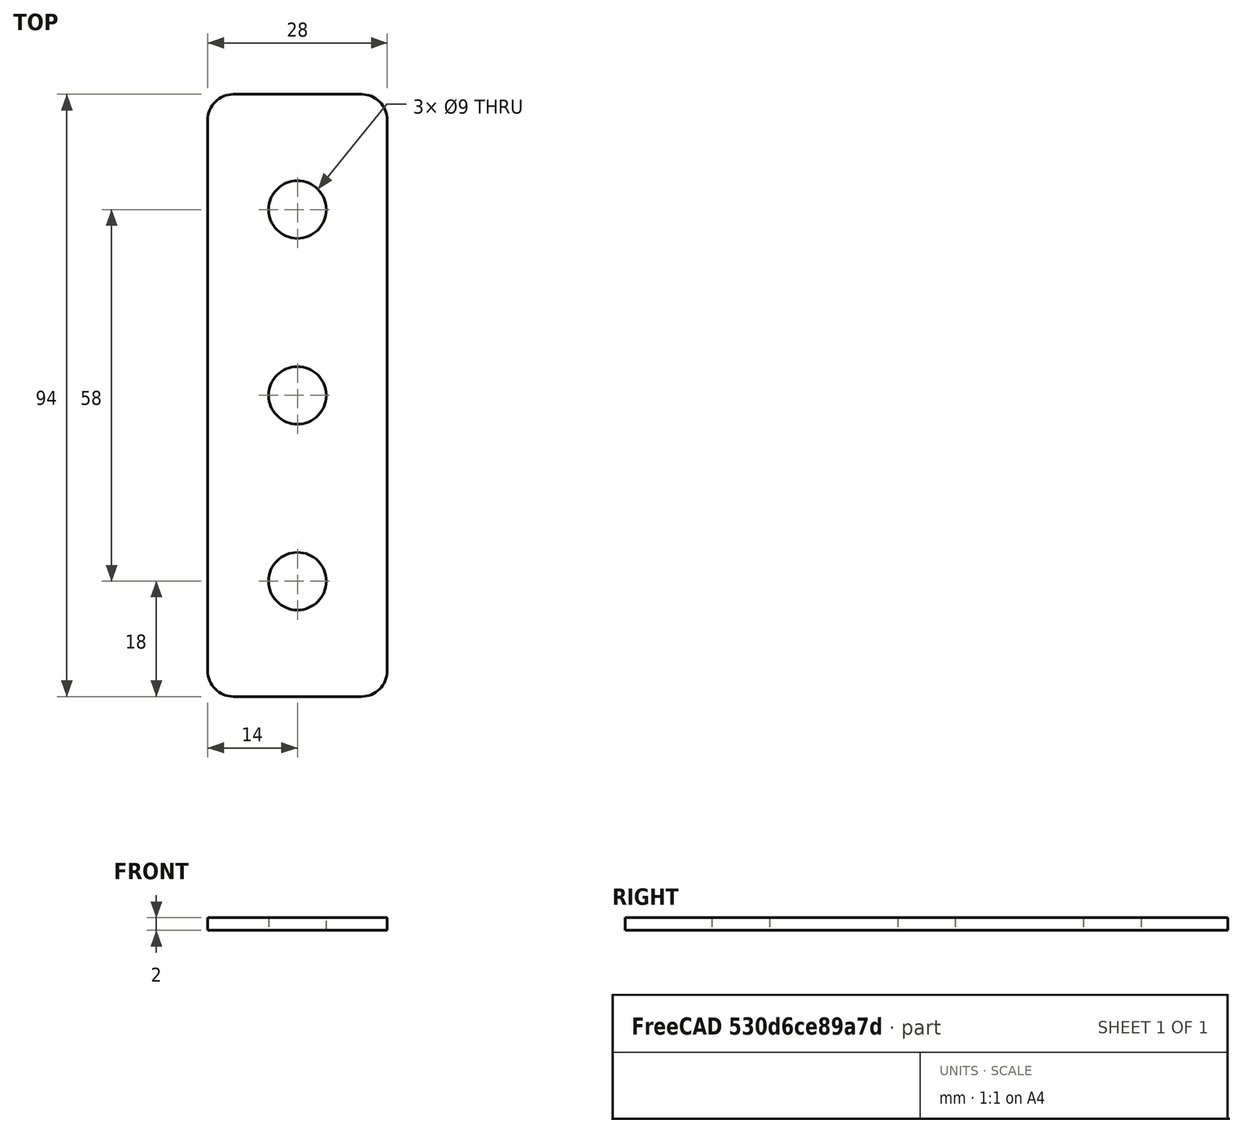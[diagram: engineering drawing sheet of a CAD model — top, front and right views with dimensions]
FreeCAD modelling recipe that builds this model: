
FCSTD DOCUMENT  (FreeCAD 0.21R33694 (Git))
Label: GabaritoCorteBorracha1
License: All rights reserved
LicenseURL: http://en.wikipedia.org/wiki/All_rights_reserved
objects: Sketcher::SketchObject×1, PartDesign::Pad×1, PartDesign::Body×1
note: 4 computed .brp shape members not serialized (recipe doc carries the construction recipe); baked Part::Feature solids carry a one-line shape summary decoded from their .brp

FEATURE [Sketcher::SketchObject] Sketch
  FullyConstrained = true
  MapMode = 5
  Support = -> [XY_Plane]
  sketch-geometry (11):
    g0: LineSegment StartX=-10 StartY=47 StartZ=0 EndX=10 EndY=47 EndZ=0
    g1: LineSegment StartX=14 StartY=43 StartZ=0 EndX=14 EndY=-43 EndZ=0
    g2: LineSegment StartX=10 StartY=-47 StartZ=0 EndX=-10 EndY=-47 EndZ=0
    g3: LineSegment StartX=-14 StartY=-43 StartZ=0 EndX=-14 EndY=43 EndZ=0
    g4: ArcOfCircle CenterX=-10 CenterY=43 CenterZ=0 NormalX=0 NormalY=0 NormalZ=1 AngleXU=0 Radius=4 StartAngle=1.5708 EndAngle=3.14159
    g5: ArcOfCircle CenterX=10 CenterY=43 CenterZ=0 NormalX=0 NormalY=0 NormalZ=1 AngleXU=0 Radius=4 StartAngle=-9e-16 EndAngle=1.5708
    g6: ArcOfCircle CenterX=10 CenterY=-43 CenterZ=0 NormalX=0 NormalY=0 NormalZ=1 AngleXU=0 Radius=4 StartAngle=4.71239 EndAngle=6.28319
    g7: ArcOfCircle CenterX=-10 CenterY=-43 CenterZ=0 NormalX=0 NormalY=0 NormalZ=1 AngleXU=0 Radius=4 StartAngle=3.14159 EndAngle=4.71239
    g8: Circle CenterX=0 CenterY=0 CenterZ=0 NormalX=0 NormalY=0 NormalZ=1 AngleXU=0 Radius=4.5
    g9: Circle CenterX=0 CenterY=29 CenterZ=0 NormalX=0 NormalY=0 NormalZ=1 AngleXU=0 Radius=4.5
    g10: Circle CenterX=0 CenterY=-29 CenterZ=0 NormalX=0 NormalY=0 NormalZ=1 AngleXU=0 Radius=4.5
  constraints (25):
    c: Horizontal(g2)
    c: Vertical(g3)
    c: Tangent(g0,g4) = 1.5708
    c: Tangent(g3,g4) = 1.5708
    c: Tangent(g0,g5) = 1.5708
    c: Tangent(g1,g5) = 1.5708
    c: Tangent(g1,g6) = 1.5708
    c: Tangent(g2,g6) = 1.5708
    c: Tangent(g2,g7) = 1.5708
    c: Tangent(g3,g7) = 1.5708
    c: Equal(g4,g5)
    c: Equal(g4,g6)
    c: Diameter(g4) = 8
    c: Horizontal(g0)
    c: Symmetric(g7,g6,g-2)
    c: Symmetric(g5,g6,g-1)
    c: DistanceY(g2,g0) = 94
    c: DistanceX(g3,g1) = 28
    c: Coincident(g8,g-1)
    c: Diameter(g8) = 9
    c: PointOnObject(g9,g-2)
    c: Symmetric(g9,g10,g-1)
    c: Equal(g9,g10)
    c: Equal(g10,g8)
    c: DistanceY(g8,g9) = 29
FEATURE [PartDesign::Pad] Pad
  Direction = (0,0,1)
  Length = 2
  Length2 = 10
  Profile = -> Sketch
  ReferenceAxis = -> Sketch [N_Axis]
  Type = 0
FEATURE [PartDesign::Body] Body
  Group = -> [Sketch,Pad]
  Origin = -> Origin
  Tip = -> Pad
